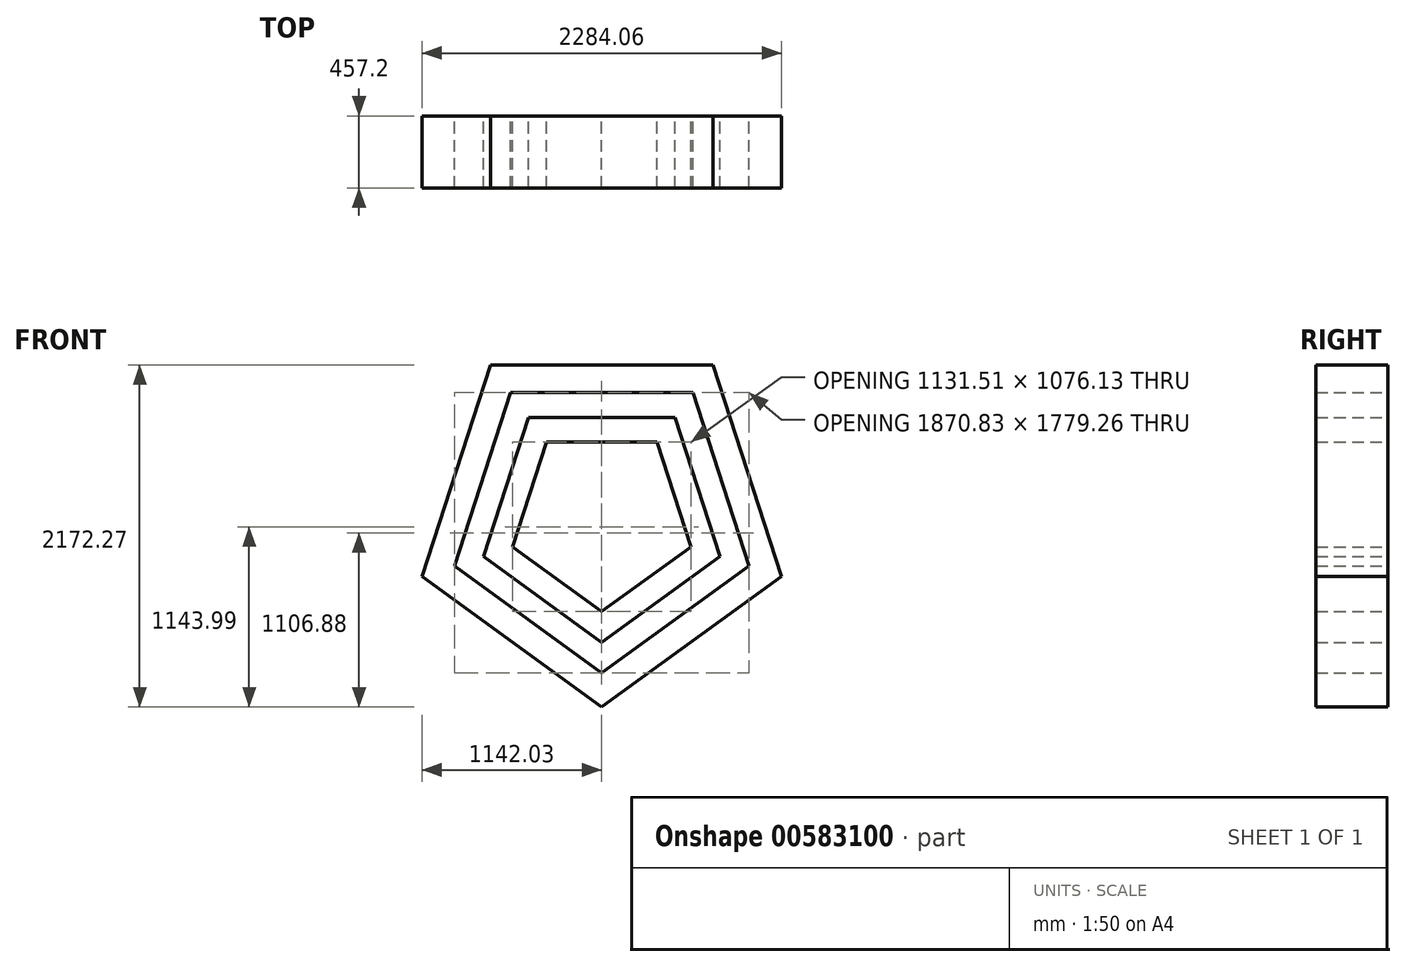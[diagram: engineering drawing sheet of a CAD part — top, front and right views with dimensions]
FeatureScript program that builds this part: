
annotation { "Feature Type Name" : "Feature", "Feature Type Description" : "" }
export const myFeature = defineFeature(function(context is Context, id is Id, definition is map)
    precondition{}
    {
        {
            var Q0;
            Q0=qCreatedBy(makeId("Front.planeOp"),FACE);
            var sketch = newSketch(context, id + "F0", { "sketchPlane" : qUnion([Q0])});
            skCircle(sketch, "E0.cCircle", {"center": v(0, 0) * mm, "radius": 1200.8 * mm, "construction": true});
            skLineSegment(sketch, "E0.0", {"start": v(0, -1200.8) * mm, "end": v(-1142.03, -371.07) * mm});
            skLineSegment(sketch, "E0.1", {"start": v(-1142.03, -371.07) * mm, "end": v(-705.81, 971.47) * mm});
            skLineSegment(sketch, "E0.2", {"start": v(-705.81, 971.47) * mm, "end": v(705.81, 971.47) * mm});
            skLineSegment(sketch, "E0.3", {"start": v(705.81, 971.47) * mm, "end": v(1142.03, -371.07) * mm});
            skLineSegment(sketch, "E0.4", {"start": v(1142.03, -371.07) * mm, "end": v(0, -1200.8) * mm});
            skCircle(sketch, "E1.cCircle", {"center": v(0, 0) * mm, "radius": 983.55 * mm, "construction": true});
            skLineSegment(sketch, "E1.0", {"start": v(0, -983.55) * mm, "end": v(-935.41, -303.93) * mm});
            skLineSegment(sketch, "E1.1", {"start": v(-935.41, -303.93) * mm, "end": v(-578.12, 795.7) * mm});
            skLineSegment(sketch, "E1.2", {"start": v(-578.12, 795.7) * mm, "end": v(578.12, 795.7) * mm});
            skLineSegment(sketch, "E1.3", {"start": v(578.12, 795.7) * mm, "end": v(935.41, -303.93) * mm});
            skLineSegment(sketch, "E1.4", {"start": v(935.41, -303.93) * mm, "end": v(0, -983.55) * mm});
            skCircle(sketch, "E2.cCircle", {"center": v(0, 0) * mm, "radius": 789.21 * mm, "construction": true});
            skLineSegment(sketch, "E2.0", {"start": v(0, -789.21) * mm, "end": v(-750.58, -243.88) * mm});
            skLineSegment(sketch, "E2.1", {"start": v(-750.58, -243.88) * mm, "end": v(-463.89, 638.49) * mm});
            skLineSegment(sketch, "E2.2", {"start": v(-463.89, 638.49) * mm, "end": v(463.89, 638.49) * mm});
            skLineSegment(sketch, "E2.3", {"start": v(463.89, 638.49) * mm, "end": v(750.58, -243.88) * mm});
            skLineSegment(sketch, "E2.4", {"start": v(750.58, -243.88) * mm, "end": v(0, -789.21) * mm});
            skCircle(sketch, "E3.cCircle", {"center": v(0, 0) * mm, "radius": 594.87 * mm, "construction": true});
            skLineSegment(sketch, "E3.0", {"start": v(0, -594.87) * mm, "end": v(-565.76, -183.83) * mm});
            skLineSegment(sketch, "E3.1", {"start": v(-565.76, -183.83) * mm, "end": v(-349.66, 481.26) * mm});
            skLineSegment(sketch, "E3.2", {"start": v(-349.66, 481.26) * mm, "end": v(349.66, 481.26) * mm});
            skLineSegment(sketch, "E3.3", {"start": v(349.66, 481.26) * mm, "end": v(565.76, -183.83) * mm});
            skLineSegment(sketch, "E3.4", {"start": v(565.76, -183.83) * mm, "end": v(0, -594.87) * mm});
            skCircle(sketch, "E4.cCircle", {"center": v(0, 0) * mm, "radius": 428.97 * mm, "construction": true});
            skLineSegment(sketch, "E4.0", {"start": v(0, -428.97) * mm, "end": v(-407.98, -132.56) * mm});
            skLineSegment(sketch, "E4.1", {"start": v(-407.98, -132.56) * mm, "end": v(-252.14, 347.04) * mm});
            skLineSegment(sketch, "E4.2", {"start": v(-252.14, 347.04) * mm, "end": v(252.14, 347.04) * mm});
            skLineSegment(sketch, "E4.3", {"start": v(252.14, 347.04) * mm, "end": v(407.98, -132.56) * mm});
            skLineSegment(sketch, "E4.4", {"start": v(407.98, -132.56) * mm, "end": v(0, -428.97) * mm});
            skCircle(sketch, "E5.cCircle", {"center": v(0, 0) * mm, "radius": 296.25 * mm, "construction": true});
            skLineSegment(sketch, "E5.0", {"start": v(0, -296.25) * mm, "end": v(-281.75, -91.55) * mm});
            skLineSegment(sketch, "E5.1", {"start": v(-281.75, -91.55) * mm, "end": v(-174.13, 239.67) * mm});
            skLineSegment(sketch, "E5.2", {"start": v(-174.13, 239.67) * mm, "end": v(174.13, 239.67) * mm});
            skLineSegment(sketch, "E5.3", {"start": v(174.13, 239.67) * mm, "end": v(281.75, -91.55) * mm});
            skLineSegment(sketch, "E5.4", {"start": v(281.75, -91.55) * mm, "end": v(0, -296.25) * mm});
            skSolve(sketch);
        }
        {
            var Q0;
            Q0=makeQuery(id+"F0.imprint","IMPRINT",FACE,{"disambiguationData":[TD([[makeQuery(id+"F0.imprint","IMPRINT",EDGE,{"derivedFrom":sQuery(id+"F0.wireOp",EDGE,"E0.0")}),-1.0]])]});
            extrude(context, id + "F1", {"entities" : qUnion([Q0]), "depth" : 457.2 * mm, "offsetDistance" : 30.48 * mm});
        }
        {
            var Q0;
            Q0=makeQuery(id+"F0.imprint","IMPRINT",FACE,{"disambiguationData":[TD([[makeQuery(id+"F0.imprint","IMPRINT",EDGE,{"derivedFrom":sQuery(id+"F0.wireOp",EDGE,"E2.0")}),-1.0]])]});
            extrude(context, id + "F2", {"entities" : qUnion([Q0]), "depth" : 457.2 * mm, "offsetDistance" : 30.48 * mm});
        }
        {
            var Q0;
            Q0=makeQuery(id+"F0.imprint","IMPRINT",FACE,{"disambiguationData":[TD([[makeQuery(id+"F0.imprint","IMPRINT",EDGE,{"derivedFrom":sQuery(id+"F0.wireOp",EDGE,"E4.0")}),-1.0]])]});
            extrude(context, id + "F3", {"entities" : qUnion([Q0]), "operationType" : NewBodyOperationType.REMOVE, "depth" : 457.2 * mm, "offsetDistance" : 30.48 * mm});
        }
    });
